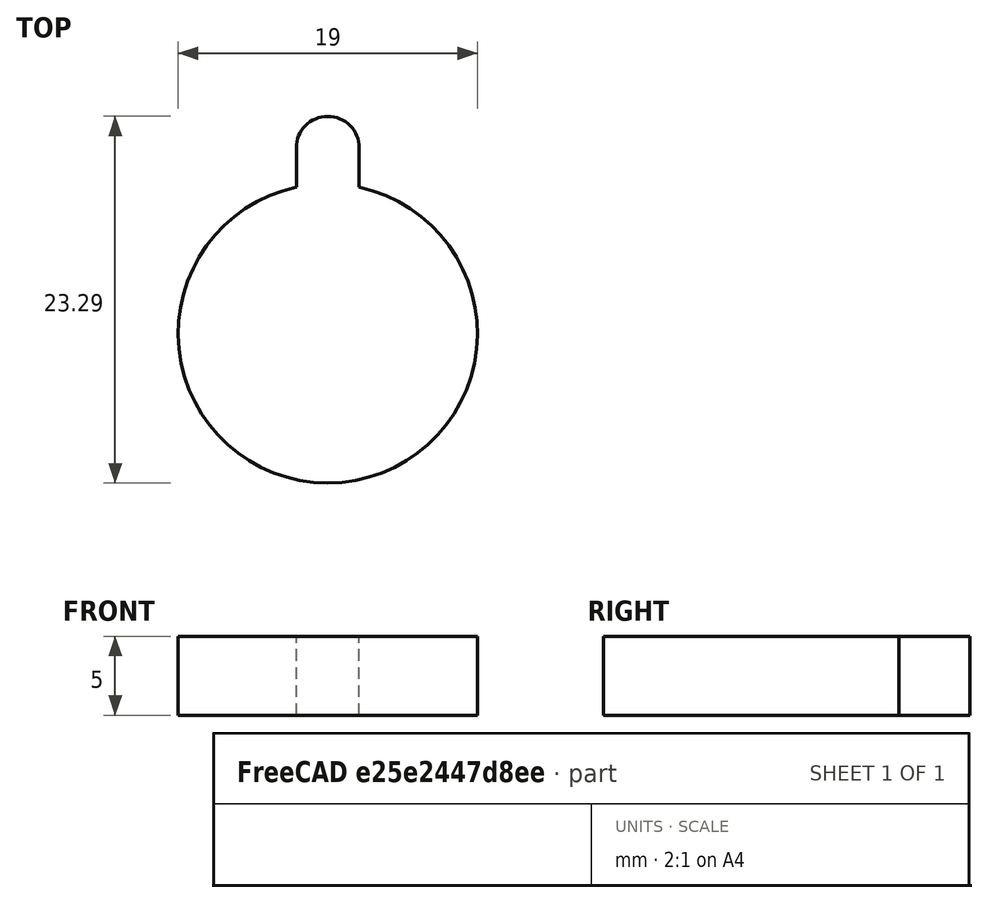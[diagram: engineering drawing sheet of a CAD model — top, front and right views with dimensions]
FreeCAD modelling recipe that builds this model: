
FCSTD DOCUMENT  (FreeCAD 0.21R33771 (Git))
Label: Trim
License: All rights reserved
LicenseURL: http://en.wikipedia.org/wiki/All_rights_reserved
objects: Sketcher::SketchObject×1, PartDesign::Pad×1, PartDesign::Body×1
note: 4 computed .brp shape members not serialized (recipe doc carries the construction recipe); baked Part::Feature solids carry a one-line shape summary decoded from their .brp

FEATURE [Sketcher::SketchObject] Sketch
  FullyConstrained = true
  MapMode = 5
  Support = -> [XY_Plane]
  sketch-geometry (5):
    g0: ArcOfCircle CenterX=0 CenterY=0 CenterZ=0 NormalX=0 NormalY=0 NormalZ=1 AngleXU=0 Radius=9.5 StartAngle=1.78291 EndAngle=7.64187
    g1: LineSegment StartX=-2 StartY=9.28709 StartZ=0 EndX=-2 EndY=11.7871 EndZ=0
    g2: ArcOfCircle CenterX=0 CenterY=11.7871 CenterZ=0 NormalX=0 NormalY=0 NormalZ=1 AngleXU=0 Radius=2 StartAngle=1.5708 EndAngle=3.14159
    g3: LineSegment StartX=2 StartY=9.28709 StartZ=0 EndX=2 EndY=11.7871 EndZ=0
    g4: ArcOfCircle CenterX=0 CenterY=11.7871 CenterZ=0 NormalX=0 NormalY=0 NormalZ=1 AngleXU=0 Radius=2 StartAngle=2.82333e-09 EndAngle=1.5708
  constraints (16):
    c: Coincident(g0,g-1)
    c: Diameter(g0) = 19
    c: Vertical(g1)
    c: DistanceY(g1,g1) = 2.5
    c: DistanceX(g1,g-1) = 2
    c: PointOnObject(g2,g-2)
    c: Coincident(g2,g1)
    c: PointOnObject(g2,g-2)
    c: Diameter(g2) = 4
    c: Vertical(g3)
    c: Coincident(g4,g3)
    c: Coincident(g4,g2)
    c: Horizontal(g1,g3)
    c: Coincident(g4,g2)
    c: Coincident(g0,g3)
    c: Coincident(g0,g1)
FEATURE [PartDesign::Pad] Pad
  Direction = (0,0,1)
  Length = 5
  Length2 = 10
  Profile = -> Sketch
  ReferenceAxis = -> Sketch [N_Axis]
  Type = 0
FEATURE [PartDesign::Body] Body
  Group = -> [Sketch,Pad]
  Origin = -> Origin
  Tip = -> Pad
